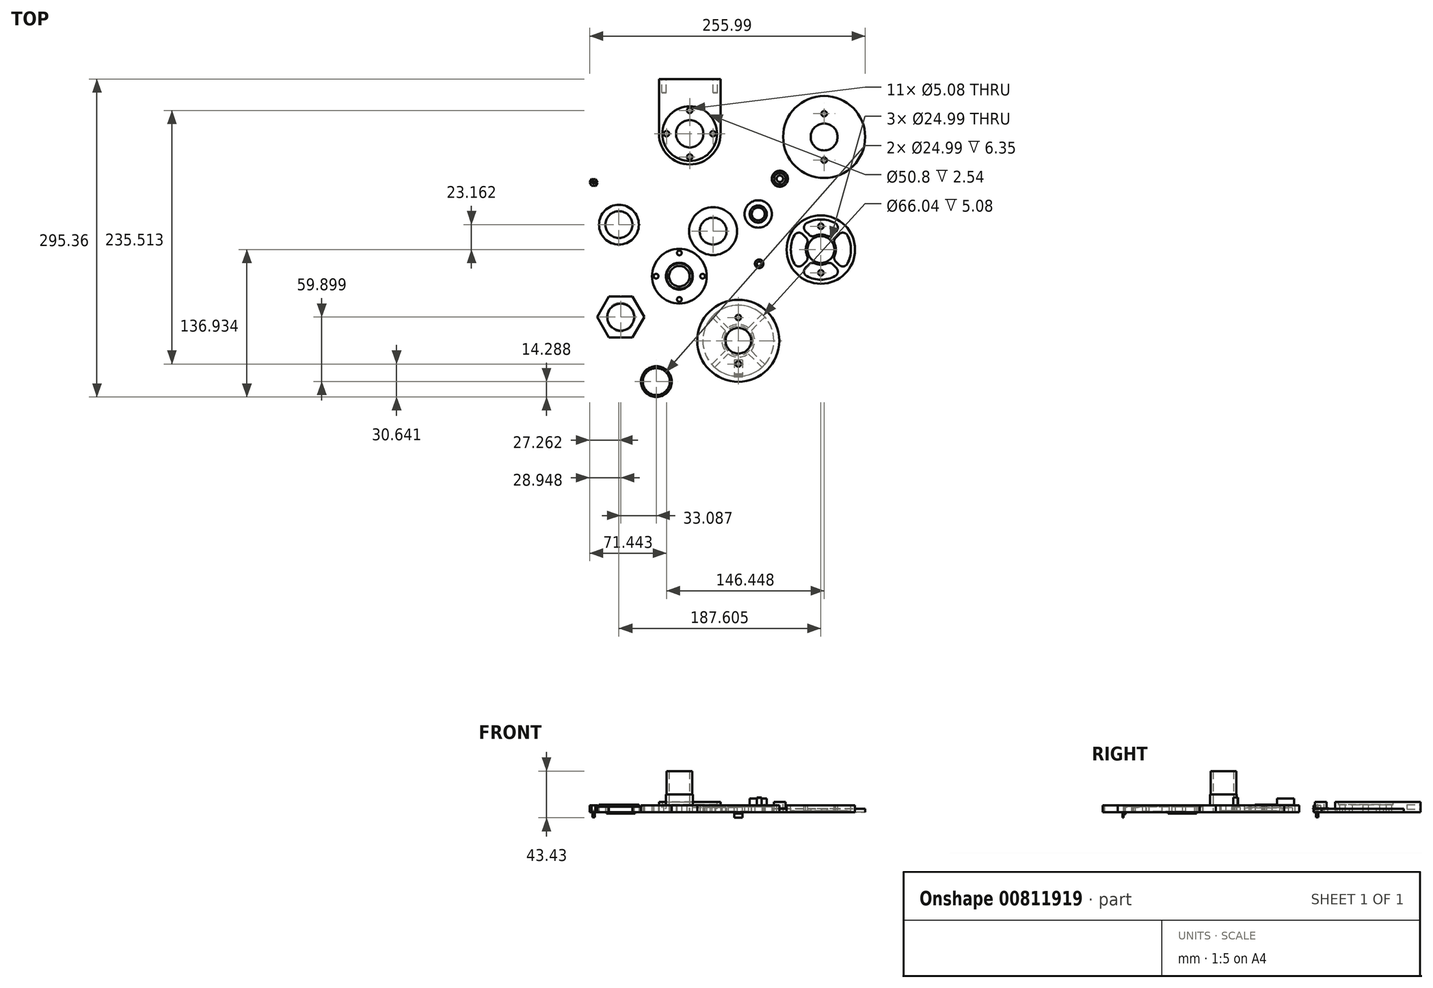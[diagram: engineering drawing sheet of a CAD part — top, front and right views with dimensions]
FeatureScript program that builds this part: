
annotation { "Feature Type Name" : "Feature", "Feature Type Description" : "" }
export const myFeature = defineFeature(function(context is Context, id is Id, definition is map)
    precondition{}
    {
        {
            var Q0;
            Q0=qCreatedBy(makeId("Top.planeOp"),FACE);
            var sketch = newSketch(context, id + "F0", { "sketchPlane" : qUnion([Q0])});
            skCircle(sketch, "E0", {"center": v(0, 0) * mm, "radius": 25.4 * mm});
            skSolve(sketch);
        }
        {
            var Q0;
            Q0=makeQuery(id+"F0.imprint","IMPRINT",FACE,{"disambiguationData":[TD([[makeQuery(id+"F0.imprint","IMPRINT",EDGE,{"derivedFrom":sQuery(id+"F0.wireOp",EDGE,"E0")}),1.0]])]});
            extrude(context, id + "F1", {"entities" : qUnion([Q0]), "depth" : 6.35 * mm});
        }
        {
            var Q0;
            Q0=makeQuery(id+"F1.opExtrude","CAP_FACE",FACE,{"disambiguationData":[OSD([sQuery(id+"F0.wireOp",EDGE,"E0")])],"isStart":false});
            var sketch = newSketch(context, id + "F2", { "sketchPlane" : qUnion([Q0])});
            skCircle(sketch, "E1", {"center": v(0, 0) * mm, "radius": 12.5 * mm});
            skSolve(sketch);
        }
        {
            var Q0;
            Q0=makeQuery(id+"F2.imprint","IMPRINT",FACE,{"disambiguationData":[TD([[makeQuery(id+"F2.imprint","IMPRINT",EDGE,{"derivedFrom":sQuery(id+"F2.wireOp",EDGE,"E1")}),1.0]])]});
            extrude(context, id + "F3", {"entities" : qUnion([Q0]), "operationType" : NewBodyOperationType.ADD, "depth" : 10.16 * mm});
        }
        {
            var Q0;
            Q0=makeQuery(id+"F3.opExtrude","CAP_FACE",FACE,{"disambiguationData":[OSD([sQuery(id+"F2.wireOp",EDGE,"E1")])],"isStart":false});
            var sketch = newSketch(context, id + "F4", { "sketchPlane" : qUnion([Q0])});
            skCircle(sketch, "E2", {"center": v(0, 0) * mm, "radius": 11.9 * mm});
            skSolve(sketch);
        }
        {
            var Q0;
            Q0=makeQuery(id+"F4.imprint","IMPRINT",FACE,{"disambiguationData":[TD([[makeQuery(id+"F4.imprint","IMPRINT",EDGE,{"derivedFrom":sQuery(id+"F4.wireOp",EDGE,"E2")}),1.0]])]});
            extrude(context, id + "F5", {"entities" : qUnion([Q0]), "operationType" : NewBodyOperationType.ADD, "depth" : 21.59 * mm});
        }
        {
            var Q0;
            Q0=makeQuery(id+"F1.opExtrude","CAP_FACE",FACE,{"disambiguationData":[OSD([sQuery(id+"F0.wireOp",EDGE,"E0")])],"isStart":true});
            var sketch = newSketch(context, id + "F6", { "sketchPlane" : qUnion([Q0])});
            skCircle(sketch, "E3", {"center": v(0, 0) * mm, "radius": 9.53 * mm});
            skSolve(sketch);
        }
        {
            var Q0;
            Q0=makeQuery(id+"F6.imprint","IMPRINT",FACE,{"disambiguationData":[TD([[makeQuery(id+"F6.imprint","IMPRINT",EDGE,{"derivedFrom":sQuery(id+"F6.wireOp",EDGE,"E3")}),1.0]])]});
            extrude(context, id + "F7", {"entities" : qUnion([Q0]), "operationType" : NewBodyOperationType.REMOVE, "endBound" : BoundingType.THROUGH_ALL, "oppositeDirection" : true, "depth" : 25.4 * mm});
        }
        {
            var Q0;
            Q0=makeQuery(id+"F1.opExtrude","CAP_FACE",FACE,{"disambiguationData":[OSD([sQuery(id+"F0.wireOp",EDGE,"E0")])],"isStart":true});
            var sketch = newSketch(context, id + "F8", { "sketchPlane" : qUnion([Q0])});
            skCircle(sketch, "E4", {"center": v(0, 0) * mm, "radius": 21.59 * mm, "construction": true});
            skCircle(sketch, "E5", {"center": v(0, -21.59) * mm, "radius": 2.16 * mm});
            skCircle(sketch, "E6", {"center": v(0, 21.59) * mm, "radius": 2.16 * mm});
            skCircle(sketch, "E7", {"center": v(-21.59, 0) * mm, "radius": 2.16 * mm});
            skCircle(sketch, "E8", {"center": v(21.59, 0) * mm, "radius": 2.16 * mm});
            skSolve(sketch);
        }
        {
            var Q0;
            {Q0=qUnion([makeQuery(id+"F8.imprint","IMPRINT",FACE,{"disambiguationData":[TD([[makeQuery(id+"F8.imprint","IMPRINT",EDGE,{"derivedFrom":sQuery(id+"F8.wireOp",EDGE,"E5")}),1.0]])]}),makeQuery(id+"F8.imprint","IMPRINT",FACE,{"disambiguationData":[TD([[makeQuery(id+"F8.imprint","IMPRINT",EDGE,{"derivedFrom":sQuery(id+"F8.wireOp",EDGE,"E8")}),1.0]])]}),makeQuery(id+"F8.imprint","IMPRINT",FACE,{"disambiguationData":[TD([[makeQuery(id+"F8.imprint","IMPRINT",EDGE,{"derivedFrom":sQuery(id+"F8.wireOp",EDGE,"E7")}),1.0]])]}),makeQuery(id+"F8.imprint","IMPRINT",FACE,{"disambiguationData":[TD([[makeQuery(id+"F8.imprint","IMPRINT",EDGE,{"derivedFrom":sQuery(id+"F8.wireOp",EDGE,"E6")}),1.0]])]})]);}
            extrude(context, id + "F9", {"entities" : qUnion([Q0]), "operationType" : NewBodyOperationType.REMOVE, "endBound" : BoundingType.THROUGH_ALL, "oppositeDirection" : true, "depth" : 25.4 * mm});
        }
        {
            var Q0;
            Q0=qCreatedBy(makeId("Top.planeOp"),FACE);
            var sketch = newSketch(context, id + "F10", { "sketchPlane" : qUnion([Q0])});
            skCircle(sketch, "E9", {"center": v(31.37, 41.87) * mm, "radius": 12.5 * mm});
            skCircle(sketch, "E10", {"center": v(31.37, 41.87) * mm, "radius": 22.23 * mm});
            skSolve(sketch);
        }
        {
            var Q0;
            Q0=makeQuery(id+"F10.imprint","IMPRINT",FACE,{"disambiguationData":[TD([[makeQuery(id+"F10.imprint","IMPRINT",EDGE,{"derivedFrom":sQuery(id+"F10.wireOp",EDGE,"E9")}),-1.0]])]});
            extrude(context, id + "F11", {"entities" : qUnion([Q0]), "depth" : 4 * mm});
        }
        {
            var Q0;
            Q0=qCreatedBy(makeId("Top.planeOp"),FACE);
            var sketch = newSketch(context, id + "F12", { "sketchPlane" : qUnion([Q0])});
            skCircle(sketch, "E11", {"center": v(-56.12, 47.92) * mm, "radius": 12.5 * mm});
            skCircle(sketch, "E12", {"center": v(-56.12, 47.92) * mm, "radius": 18.5 * mm});
            skSolve(sketch);
        }
        {
            var Q0;
            Q0=makeQuery(id+"F12.imprint","IMPRINT",FACE,{"disambiguationData":[TD([[makeQuery(id+"F12.imprint","IMPRINT",EDGE,{"derivedFrom":sQuery(id+"F12.wireOp",EDGE,"E11")}),-1.0]])]});
            extrude(context, id + "F13", {"entities" : qUnion([Q0]), "depth" : 7 * mm});
        }
        {
            var Q0;
            Q0=makeQuery(id+"F13.opExtrude","CAP_FACE",FACE,{"disambiguationData":[OSD([sQuery(id+"F12.wireOp",EDGE,"E11"),sQuery(id+"F12.wireOp",EDGE,"E12")])],"isStart":false});
            var Q1;
            Q1=makeQuery(id+"F13.opExtrude","SWEPT_FACE",FACE,{"disambiguationData":[OSD([sQuery(id+"F12.wireOp",EDGE,"E11")])]});
            var Q2;
            Q2=makeQuery(id+"F13.opExtrude","SWEPT_FACE",FACE,{"disambiguationData":[OSD([sQuery(id+"F12.wireOp",EDGE,"E12")])]});
            var Q3;
            Q3=makeQuery(id+"F13.opExtrude","CAP_FACE",FACE,{"disambiguationData":[OSD([sQuery(id+"F12.wireOp",EDGE,"E11"),sQuery(id+"F12.wireOp",EDGE,"E12")])],"isStart":true});
            fillet(context, id + "F14", {"entities" : qUnion([Q0, Q1, Q2, Q3]), "radius" : 0.64 * mm, "tangentPropagation" : true, "allowEdgeOverflow" : false});
        }
        {
            var Q0;
            Q0=qCreatedBy(makeId("Top.planeOp"),FACE);
            var sketch = newSketch(context, id + "F15", { "sketchPlane" : qUnion([Q0])});
            skLineSegment(sketch, "E13", {"start": v(-76.43, -38) * mm, "end": v(-65.43, -18.94) * mm});
            skLineSegment(sketch, "E14", {"start": v(-65.43, -18.94) * mm, "end": v(-43.43, -18.94) * mm});
            skLineSegment(sketch, "E15", {"start": v(-43.43, -18.94) * mm, "end": v(-32.44, -38) * mm});
            skLineSegment(sketch, "E16", {"start": v(-32.44, -38) * mm, "end": v(-43.43, -57.04) * mm});
            skLineSegment(sketch, "E17", {"start": v(-43.43, -57.04) * mm, "end": v(-65.43, -57.04) * mm});
            skLineSegment(sketch, "E18", {"start": v(-65.43, -57.04) * mm, "end": v(-76.43, -38) * mm});
            skSolve(sketch);
        }
        {
            var Q0;
            Q0=makeQuery(id+"F15.imprint","IMPRINT",FACE,{"disambiguationData":[TD([[makeQuery(id+"F15.imprint","IMPRINT",EDGE,{"derivedFrom":sQuery(id+"F15.wireOp",EDGE,"E13")}),-1.0]])]});
            extrude(context, id + "F16", {"entities" : qUnion([Q0]), "depth" : 5.08 * mm});
        }
        {
            var Q0;
            Q0=makeQuery(id+"F16.opExtrude","CAP_FACE",FACE,{"disambiguationData":[OSD([sQuery(id+"F15.wireOp",EDGE,"E13"),sQuery(id+"F15.wireOp",EDGE,"E14"),sQuery(id+"F15.wireOp",EDGE,"E15"),sQuery(id+"F15.wireOp",EDGE,"E16"),sQuery(id+"F15.wireOp",EDGE,"E17"),sQuery(id+"F15.wireOp",EDGE,"E18")])],"isStart":true});
            var sketch = newSketch(context, id + "F17", { "sketchPlane" : qUnion([Q0])});
            skCircle(sketch, "E19", {"center": v(-54.43, 38) * mm, "radius": 12.5 * mm});
            skSolve(sketch);
        }
        {
            var Q0;
            Q0=makeQuery(id+"F17.imprint","IMPRINT",FACE,{"disambiguationData":[TD([[makeQuery(id+"F17.imprint","IMPRINT",EDGE,{"derivedFrom":sQuery(id+"F17.wireOp",EDGE,"E19")}),1.0]])]});
            extrude(context, id + "F18", {"entities" : qUnion([Q0]), "operationType" : NewBodyOperationType.REMOVE, "endBound" : BoundingType.THROUGH_ALL, "oppositeDirection" : true, "depth" : 25.4 * mm});
        }
        {
            var Q0;
            Q0=makeQuery(id+"F16.opExtrude","CAP_FACE",FACE,{"disambiguationData":[OSD([sQuery(id+"F15.wireOp",EDGE,"E13"),sQuery(id+"F15.wireOp",EDGE,"E14"),sQuery(id+"F15.wireOp",EDGE,"E15"),sQuery(id+"F15.wireOp",EDGE,"E16"),sQuery(id+"F15.wireOp",EDGE,"E17"),sQuery(id+"F15.wireOp",EDGE,"E18")])],"isStart":true});
            var sketch = newSketch(context, id + "F19", { "sketchPlane" : qUnion([Q0])});
            skCircle(sketch, "E20", {"center": v(-54.43, 38) * mm, "radius": 13.34 * mm});
            skSolve(sketch);
        }
        {
            var Q0;
            Q0=makeQuery(id+"F19.imprint","IMPRINT",FACE,{"disambiguationData":[TD([[makeQuery(id+"F19.imprint","IMPRINT",EDGE,{"derivedFrom":sQuery(id+"F19.wireOp",EDGE,"E20")}),1.0]])]});
            extrude(context, id + "F20", {"entities" : qUnion([Q0]), "operationType" : NewBodyOperationType.ADD, "depth" : 1.27 * mm});
        }
        {
            var Q0;
            Q0=qCreatedBy(makeId("Top.planeOp"),FACE);
            var sketch = newSketch(context, id + "F21", { "sketchPlane" : qUnion([Q0])});
            skCircle(sketch, "E21", {"center": v(54.8, -59.95) * mm, "radius": 11.9 * mm});
            skCircle(sketch, "E22", {"center": v(54.8, -59.95) * mm, "radius": 38.1 * mm});
            skSolve(sketch);
        }
        {
            var Q0;
            Q0=makeQuery(id+"F21.imprint","IMPRINT",FACE,{"disambiguationData":[TD([[makeQuery(id+"F21.imprint","IMPRINT",EDGE,{"derivedFrom":sQuery(id+"F21.wireOp",EDGE,"E21")}),-1.0]])]});
            extrude(context, id + "F22", {"entities" : qUnion([Q0]), "depth" : 6.35 * mm});
        }
        {
            var Q0;
            Q0=qCreatedBy(makeId("Top.planeOp"),FACE);
            var sketch = newSketch(context, id + "F23", { "sketchPlane" : qUnion([Q0])});
            skCircle(sketch, "E23", {"center": v(73.3, 57.82) * mm, "radius": 12.7 * mm});
            skSolve(sketch);
        }
        {
            var Q0;
            Q0=makeQuery(id+"F23.imprint","IMPRINT",FACE,{"disambiguationData":[TD([[makeQuery(id+"F23.imprint","IMPRINT",EDGE,{"derivedFrom":sQuery(id+"F23.wireOp",EDGE,"E23")}),1.0]])]});
            extrude(context, id + "F24", {"entities" : qUnion([Q0]), "depth" : 6.35 * mm});
        }
        {
            var Q0;
            Q0=makeQuery(id+"F24.opExtrude","CAP_FACE",FACE,{"disambiguationData":[OSD([sQuery(id+"F23.wireOp",EDGE,"E23")])],"isStart":false});
            var sketch = newSketch(context, id + "F25", { "sketchPlane" : qUnion([Q0])});
            skCircle(sketch, "E24", {"center": v(73.3, 57.82) * mm, "radius": 7.94 * mm});
            skSolve(sketch);
        }
        {
            var Q0;
            Q0=makeQuery(id+"F25.imprint","IMPRINT",FACE,{"disambiguationData":[TD([[makeQuery(id+"F25.imprint","IMPRINT",EDGE,{"derivedFrom":sQuery(id+"F25.wireOp",EDGE,"E24")}),1.0]])]});
            extrude(context, id + "F26", {"entities" : qUnion([Q0]), "operationType" : NewBodyOperationType.ADD, "depth" : 6.35 * mm});
        }
        {
            var Q0;
            Q0=qCreatedBy(makeId("Top.planeOp"),FACE);
            var sketch = newSketch(context, id + "F27", { "sketchPlane" : qUnion([Q0])});
            skCircle(sketch, "E25", {"center": v(-21.34, -97.9) * mm, "radius": 12.5 * mm});
            skCircle(sketch, "E26", {"center": v(-21.34, -97.9) * mm, "radius": 14.29 * mm});
            skSolve(sketch);
        }
        {
            var Q0;
            Q0=makeQuery(id+"F27.imprint","IMPRINT",FACE,{"disambiguationData":[TD([[makeQuery(id+"F27.imprint","IMPRINT",EDGE,{"derivedFrom":sQuery(id+"F27.wireOp",EDGE,"E25")}),-1.0]])]});
            extrude(context, id + "F28", {"entities" : qUnion([Q0]), "depth" : 6.35 * mm});
        }
        {
            var Q0;
            Q0=makeQuery(id+"F26.opExtrude","CAP_FACE",FACE,{"disambiguationData":[OSD([sQuery(id+"F25.wireOp",EDGE,"E24")])],"isStart":false});
            var sketch = newSketch(context, id + "F29", { "sketchPlane" : qUnion([Q0])});
            skCircle(sketch, "E27", {"center": v(73.3, 57.82) * mm, "radius": 6 * mm});
            skSolve(sketch);
        }
        {
            var Q0;
            Q0=makeQuery(id+"F29.imprint","IMPRINT",FACE,{"disambiguationData":[TD([[makeQuery(id+"F29.imprint","IMPRINT",EDGE,{"derivedFrom":sQuery(id+"F29.wireOp",EDGE,"E27")}),1.0]])]});
            extrude(context, id + "F30", {"entities" : qUnion([Q0]), "operationType" : NewBodyOperationType.REMOVE, "endBound" : BoundingType.THROUGH_ALL, "oppositeDirection" : true, "depth" : 25.4 * mm});
        }
        {
            var Q0;
            Q0=qCreatedBy(makeId("Top.planeOp"),FACE);
            var sketch = newSketch(context, id + "F31", { "sketchPlane" : qUnion([Q0])});
            skCircle(sketch, "E28", {"center": v(9.65, 132.38) * mm, "radius": 28.58 * mm});
            skCircle(sketch, "E29", {"center": v(9.65, 132.38) * mm, "radius": 12.7 * mm});
            skLineSegment(sketch, "E30.bottom", {"start": v(-18.92, 132.38) * mm, "end": v(38.23, 132.38) * mm});
            skLineSegment(sketch, "E30.top", {"start": v(-18.92, 183.18) * mm, "end": v(38.23, 183.18) * mm});
            skLineSegment(sketch, "E30.left", {"start": v(-18.92, 132.38) * mm, "end": v(-18.92, 183.18) * mm});
            skLineSegment(sketch, "E30.right", {"start": v(38.23, 132.38) * mm, "end": v(38.23, 183.18) * mm});
            skSolve(sketch);
        }
        {
            var Q0;
            {var subQ3=sQuery(id+"F31.wireOp",EDGE,"E30.bottom");var subQ7=sQuery(id+"F31.wireOp",EDGE,"E29");var subQ10=makeQuery(id+"F31.imprint","INTERSECT",VERTEX,{"disambiguationData":[OD(0.0)],"derivedFrom":[subQ7,subQ3]});Q0=qUnion([makeQuery(id+"F31.imprint","IMPRINT",FACE,{"disambiguationData":[TD([[makeQuery(id+"F31.imprint","IMPRINT",EDGE,{"derivedFrom":sQuery(id+"F31.wireOp",EDGE,"E30.top")}),-1.0]])]}),makeQuery(id+"F31.imprint","IMPRINT",FACE,{"disambiguationData":[TD([[makeQuery(id+"F31.imprint","IMPRINT",EDGE,{"disambiguationData":[TD([[subQ10,1.0]])],"derivedFrom":subQ7}),-1.0]])]}),makeQuery(id+"F31.imprint","IMPRINT",FACE,{"disambiguationData":[TD([[makeQuery(id+"F31.imprint","IMPRINT",EDGE,{"disambiguationData":[TD([[subQ10,-1.0]])],"derivedFrom":subQ7}),-1.0]])]})]);}
            extrude(context, id + "F32", {"entities" : qUnion([Q0]), "depth" : 9.52 * mm});
        }
        {
            var Q0;
            Q0=makeQuery(id+"F32.opExtrude","CAP_FACE",FACE,{"disambiguationData":[OSD([sQuery(id+"F31.wireOp",EDGE,"E28"),sQuery(id+"F31.wireOp",EDGE,"E29"),sQuery(id+"F31.wireOp",EDGE,"E30.top"),sQuery(id+"F31.wireOp",EDGE,"E30.left"),sQuery(id+"F31.wireOp",EDGE,"E30.right")])],"isStart":false});
            var sketch = newSketch(context, id + "F33", { "sketchPlane" : qUnion([Q0])});
            skCircle(sketch, "E31", {"center": v(9.65, 132.38) * mm, "radius": 25.4 * mm});
            skSolve(sketch);
        }
        {
            var Q0;
            Q0=makeQuery(id+"F33.imprint","IMPRINT",FACE,{"disambiguationData":[TD([[makeQuery(id+"F33.imprint","IMPRINT",EDGE,{"derivedFrom":sQuery(id+"F33.wireOp",EDGE,"E31")}),1.0]])]});
            extrude(context, id + "F34", {"entities" : qUnion([Q0]), "operationType" : NewBodyOperationType.REMOVE, "oppositeDirection" : true, "depth" : 2.54 * mm});
        }
        {
            var Q0;
            Q0=makeQuery(id+"F34.boolean.opBoolean","COPY",FACE,{"derivedFrom":makeQuery(id+"F34.opExtrude","CAP_FACE",FACE,{"disambiguationData":[OSD([sQuery(id+"F31.wireOp",EDGE,"E29"),sQuery(id+"F33.wireOp",EDGE,"E31")])],"isStart":false})});
            var sketch = newSketch(context, id + "F35", { "sketchPlane" : qUnion([Q0])});
            skCircle(sketch, "E32", {"center": v(9.65, 132.38) * mm, "radius": 21.59 * mm, "construction": true});
            skCircle(sketch, "E33", {"center": v(9.65, 153.97) * mm, "radius": 2.54 * mm});
            skCircle(sketch, "E34", {"center": v(31.24, 132.38) * mm, "radius": 2.54 * mm});
            skCircle(sketch, "E35", {"center": v(9.65, 110.8) * mm, "radius": 2.54 * mm});
            skCircle(sketch, "E36", {"center": v(-11.94, 132.38) * mm, "radius": 2.54 * mm});
            skLineSegment(sketch, "E37", {"start": v(-11.94, 132.38) * mm, "end": v(31.24, 132.38) * mm, "construction": true});
            skLineSegment(sketch, "E38", {"start": v(9.65, 153.97) * mm, "end": v(9.65, 110.8) * mm, "construction": true});
            skSolve(sketch);
        }
        {
            var Q0;
            {Q0=qUnion([makeQuery(id+"F35.imprint","IMPRINT",FACE,{"disambiguationData":[TD([[makeQuery(id+"F35.imprint","IMPRINT",EDGE,{"derivedFrom":sQuery(id+"F35.wireOp",EDGE,"E33")}),1.0]])]}),makeQuery(id+"F35.imprint","IMPRINT",FACE,{"disambiguationData":[TD([[makeQuery(id+"F35.imprint","IMPRINT",EDGE,{"derivedFrom":sQuery(id+"F35.wireOp",EDGE,"E34")}),1.0]])]}),makeQuery(id+"F35.imprint","IMPRINT",FACE,{"disambiguationData":[TD([[makeQuery(id+"F35.imprint","IMPRINT",EDGE,{"derivedFrom":sQuery(id+"F35.wireOp",EDGE,"E35")}),1.0]])]}),makeQuery(id+"F35.imprint","IMPRINT",FACE,{"disambiguationData":[TD([[makeQuery(id+"F35.imprint","IMPRINT",EDGE,{"derivedFrom":sQuery(id+"F35.wireOp",EDGE,"E36")}),1.0]])]})]);}
            extrude(context, id + "F36", {"entities" : qUnion([Q0]), "operationType" : NewBodyOperationType.REMOVE, "endBound" : BoundingType.THROUGH_ALL, "oppositeDirection" : true, "depth" : 25.4 * mm});
        }
        {
            var Q0;
            Q0=makeQuery(id+"F32.opExtrude","SWEPT_FACE",FACE,{"disambiguationData":[OSD([sQuery(id+"F31.wireOp",EDGE,"E30.top")])]});
            var sketch = newSketch(context, id + "F37", { "sketchPlane" : qUnion([Q0])});
            skCircle(sketch, "E39", {"center": v(14.16, 4.76) * mm, "radius": 2.16 * mm});
            skCircle(sketch, "E40", {"center": v(-33.47, 4.76) * mm, "radius": 2.16 * mm});
            skSolve(sketch);
        }
        {
            var Q0;
            {Q0=qUnion([makeQuery(id+"F37.imprint","IMPRINT",FACE,{"disambiguationData":[TD([[makeQuery(id+"F37.imprint","IMPRINT",EDGE,{"derivedFrom":sQuery(id+"F37.wireOp",EDGE,"E39")}),1.0]])]}),makeQuery(id+"F37.imprint","IMPRINT",FACE,{"disambiguationData":[TD([[makeQuery(id+"F37.imprint","IMPRINT",EDGE,{"derivedFrom":sQuery(id+"F37.wireOp",EDGE,"E40")}),1.0]])]})]);}
            extrude(context, id + "F38", {"entities" : qUnion([Q0]), "operationType" : NewBodyOperationType.REMOVE, "oppositeDirection" : true, "depth" : 12.7 * mm});
        }
        {
            var Q0;
            Q0=qCreatedBy(makeId("Top.planeOp"),FACE);
            var sketch = newSketch(context, id + "F39", { "sketchPlane" : qUnion([Q0])});
            skCircle(sketch, "E41", {"center": v(74.17, 11.52) * mm, "radius": 4 * mm});
            skSolve(sketch);
        }
        {
            var Q0;
            Q0=makeQuery(id+"F39.imprint","IMPRINT",FACE,{"disambiguationData":[TD([[makeQuery(id+"F39.imprint","IMPRINT",EDGE,{"derivedFrom":sQuery(id+"F39.wireOp",EDGE,"E41")}),1.0]])]});
            extrude(context, id + "F40", {"entities" : qUnion([Q0]), "depth" : 4.7 * mm});
        }
        {
            var Q0;
            Q0=makeQuery(id+"F40.opExtrude","CAP_FACE",FACE,{"disambiguationData":[OSD([sQuery(id+"F39.wireOp",EDGE,"E41")])],"isStart":false});
            var sketch = newSketch(context, id + "F41", { "sketchPlane" : qUnion([Q0])});
            skCircle(sketch, "E42", {"center": v(74.17, 11.52) * mm, "radius": 2.16 * mm});
            skSolve(sketch);
        }
        {
            var Q0;
            Q0=makeQuery(id+"F41.imprint","IMPRINT",FACE,{"disambiguationData":[TD([[makeQuery(id+"F41.imprint","IMPRINT",EDGE,{"derivedFrom":sQuery(id+"F41.wireOp",EDGE,"E42")}),1.0]])]});
            extrude(context, id + "F42", {"entities" : qUnion([Q0]), "operationType" : NewBodyOperationType.ADD, "depth" : 8.9 * mm});
        }
        {
            var Q0;
            Q0=makeQuery(id+"F22.opExtrude","CAP_FACE",FACE,{"disambiguationData":[OSD([sQuery(id+"F21.wireOp",EDGE,"E21"),sQuery(id+"F21.wireOp",EDGE,"E22")])],"isStart":false});
            var sketch = newSketch(context, id + "F43", { "sketchPlane" : qUnion([Q0])});
            skCircle(sketch, "E43", {"center": v(54.8, -59.95) * mm, "radius": 21.59 * mm, "construction": true});
            skCircle(sketch, "E44", {"center": v(54.8, -38.36) * mm, "radius": 2.54 * mm});
            skCircle(sketch, "E45", {"center": v(54.8, -81.54) * mm, "radius": 2.54 * mm});
            skSolve(sketch);
        }
        {
            var Q0;
            {Q0=qUnion([makeQuery(id+"F43.imprint","IMPRINT",FACE,{"disambiguationData":[TD([[makeQuery(id+"F43.imprint","IMPRINT",EDGE,{"derivedFrom":sQuery(id+"F43.wireOp",EDGE,"E45")}),1.0]])]}),makeQuery(id+"F43.imprint","IMPRINT",FACE,{"disambiguationData":[TD([[makeQuery(id+"F43.imprint","IMPRINT",EDGE,{"derivedFrom":sQuery(id+"F43.wireOp",EDGE,"E44")}),1.0]])]})]);}
            extrude(context, id + "F44", {"entities" : qUnion([Q0]), "operationType" : NewBodyOperationType.REMOVE, "endBound" : BoundingType.THROUGH_ALL, "oppositeDirection" : true, "depth" : 25.4 * mm});
        }
        {
            var Q0;
            Q0=makeQuery(id+"F22.opExtrude","CAP_FACE",FACE,{"disambiguationData":[OSD([sQuery(id+"F21.wireOp",EDGE,"E21"),sQuery(id+"F21.wireOp",EDGE,"E22")])],"isStart":true});
            var sketch = newSketch(context, id + "F45", { "sketchPlane" : qUnion([Q0])});
            skArc(sketch, "E46", {"start": v(30.13, 81.91) * mm, "mid": v(21.77, 59.95) * mm, "end": v(30.13, 37.99) * mm});
            skArc(sketch, "E47", {"start": v(42.75, 69.3) * mm, "mid": v(39.55, 59.95) * mm, "end": v(42.75, 50.6) * mm});
            skLineSegment(sketch, "E48.rect.bottom", {"start": v(78.14, 83.3) * mm, "end": v(31.44, 83.3) * mm, "construction": true});
            skLineSegment(sketch, "E48.rect.top", {"start": v(78.14, 36.6) * mm, "end": v(31.44, 36.6) * mm, "construction": true});
            skLineSegment(sketch, "E48.rect.left", {"start": v(78.14, 83.3) * mm, "end": v(78.14, 36.6) * mm, "construction": true});
            skLineSegment(sketch, "E48.rect.right", {"start": v(31.44, 83.3) * mm, "end": v(31.44, 36.6) * mm, "construction": true});
            skLineSegment(sketch, "E49", {"start": v(31.44, 83.3) * mm, "end": v(78.14, 36.6) * mm, "construction": true});
            skLineSegment(sketch, "E50", {"start": v(31.44, 36.6) * mm, "end": v(78.14, 83.3) * mm, "construction": true});
            skLineSegment(sketch, "E51.0", {"start": v(30.1, 81.95) * mm, "end": v(42.75, 69.3) * mm});
            skLineSegment(sketch, "E52.0", {"start": v(32.79, 35.25) * mm, "end": v(45.45, 47.91) * mm});
            skLineSegment(sketch, "E53.0", {"start": v(32.79, 84.64) * mm, "end": v(45.45, 71.99) * mm});
            skLineSegment(sketch, "E54.0", {"start": v(30.1, 37.95) * mm, "end": v(42.75, 50.6) * mm});
            skLineSegment(sketch, "E55.trimOffspring", {"start": v(54.8, 62.64) * mm, "end": v(57.48, 59.95) * mm});
            skLineSegment(sketch, "E56.trimOffspring", {"start": v(52.1, 59.95) * mm, "end": v(54.8, 57.25) * mm});
            skLineSegment(sketch, "E57.trimOffspring", {"start": v(64.14, 71.99) * mm, "end": v(76.8, 84.64) * mm});
            skLineSegment(sketch, "E58.trimOffspring", {"start": v(66.83, 69.3) * mm, "end": v(79.49, 81.95) * mm});
            skLineSegment(sketch, "E59.trimOffspring", {"start": v(66.83, 50.6) * mm, "end": v(79.49, 37.95) * mm});
            skLineSegment(sketch, "E60.trimOffspring", {"start": v(64.14, 47.91) * mm, "end": v(76.8, 35.25) * mm});
            skLineSegment(sketch, "E61.trimOffspring", {"start": v(54.8, 57.25) * mm, "end": v(57.48, 59.95) * mm});
            skLineSegment(sketch, "E62.trimOffspring", {"start": v(52.1, 59.95) * mm, "end": v(54.8, 62.64) * mm});
            skArc(sketch, "E63.trimOffspring", {"start": v(64.14, 71.99) * mm, "mid": v(54.8, 75.19) * mm, "end": v(45.45, 71.99) * mm});
            skArc(sketch, "E64.trimOffspring", {"start": v(66.83, 50.6) * mm, "mid": v(70.03, 59.95) * mm, "end": v(66.83, 69.3) * mm});
            skArc(sketch, "E65.trimOffspring", {"start": v(45.45, 47.91) * mm, "mid": v(54.8, 44.7) * mm, "end": v(64.14, 47.91) * mm});
            skArc(sketch, "E66.trimOffspring", {"start": v(76.75, 84.6) * mm, "mid": v(54.8, 92.97) * mm, "end": v(32.83, 84.6) * mm});
            skArc(sketch, "E67.trimOffspring", {"start": v(32.83, 35.3) * mm, "mid": v(54.8, 26.93) * mm, "end": v(76.75, 35.3) * mm});
            skArc(sketch, "E68.trimOffspring", {"start": v(79.45, 37.99) * mm, "mid": v(87.81, 59.95) * mm, "end": v(79.45, 81.91) * mm});
            skSolve(sketch);
        }
        {
            var Q0;
            {var subQ2=sQuery(id+"F45.wireOp",EDGE,"E65.trimOffspring");var subQ6=sQuery(id+"F45.wireOp",EDGE,"E64.trimOffspring");var subQ10=sQuery(id+"F45.wireOp",EDGE,"E63.trimOffspring");var subQ15=sQuery(id+"F45.wireOp",EDGE,"E46");Q0=qUnion([makeQuery(id+"F45.imprint","IMPRINT",FACE,{"disambiguationData":[TD([[makeQuery(id+"F45.imprint","IMPRINT",EDGE,{"derivedFrom":sQuery(id+"F45.wireOp",EDGE,"E55.trimOffspring")}),-1.0]])]}),makeQuery(id+"F45.imprint","IMPRINT",FACE,{"disambiguationData":[TD([[makeQuery(id+"F45.imprint","IMPRINT",EDGE,{"derivedFrom":subQ2}),-1.0]])]}),makeQuery(id+"F45.imprint","IMPRINT",FACE,{"disambiguationData":[TD([[makeQuery(id+"F45.imprint","IMPRINT",EDGE,{"derivedFrom":subQ6}),-1.0]])]}),makeQuery(id+"F45.imprint","IMPRINT",FACE,{"disambiguationData":[TD([[makeQuery(id+"F45.imprint","IMPRINT",EDGE,{"derivedFrom":subQ10}),-1.0]])]}),makeQuery(id+"F45.imprint","IMPRINT",FACE,{"disambiguationData":[TD([[makeQuery(id+"F45.imprint","IMPRINT",EDGE,{"derivedFrom":subQ15}),1.0]])]})]);}
            extrude(context, id + "F46", {"entities" : qUnion([Q0]), "operationType" : NewBodyOperationType.REMOVE, "oppositeDirection" : true, "depth" : 5.08 * mm});
        }
        {
            var Q0;
            Q0=makeQuery(id+"F22.opExtrude","CAP_FACE",FACE,{"disambiguationData":[OSD([sQuery(id+"F21.wireOp",EDGE,"E21"),sQuery(id+"F21.wireOp",EDGE,"E22")])],"isStart":true});
            var sketch = newSketch(context, id + "F47", { "sketchPlane" : qUnion([Q0])});
            skCircle(sketch, "E69", {"center": v(54.8, 59.95) * mm, "radius": 13.65 * mm});
            skCircle(sketch, "E70", {"center": v(54.8, 59.95) * mm, "radius": 33.02 * mm});
            skSolve(sketch);
        }
        {
            var Q0;
            {var subQ4=makeQuery(id+"F47.imprint","IMPRINT",EDGE,{"derivedFrom":makeQuery(id+"F46.boolean.opBoolean","COPY",EDGE,{"derivedFrom":makeQuery(id+"F46.opExtrude","CAP_EDGE",EDGE,{"disambiguationData":[OSD([sQuery(id+"F45.wireOp",EDGE,"E47")])],"isStart":true})})});var subQ11=makeQuery(id+"F46.boolean.opBoolean","COPY",EDGE,{"derivedFrom":makeQuery(id+"F46.opExtrude","CAP_EDGE",EDGE,{"disambiguationData":[OSD([sQuery(id+"F45.wireOp",EDGE,"E58.trimOffspring")])],"isStart":true})});var subQ12=makeQuery(id+"F47.imprint","IMPRINT",EDGE,{"derivedFrom":subQ11});var subQ18=makeQuery(id+"F46.boolean.opBoolean","COPY",EDGE,{"derivedFrom":makeQuery(id+"F46.opExtrude","CAP_EDGE",EDGE,{"disambiguationData":[OSD([sQuery(id+"F45.wireOp",EDGE,"E52.0")])],"isStart":true})});var subQ19=makeQuery(id+"F47.imprint","IMPRINT",EDGE,{"derivedFrom":subQ18});var subQ25=makeQuery(id+"F46.boolean.opBoolean","COPY",EDGE,{"derivedFrom":makeQuery(id+"F46.opExtrude","CAP_EDGE",EDGE,{"disambiguationData":[OSD([sQuery(id+"F45.wireOp",EDGE,"E53.0")])],"isStart":true})});var subQ26=makeQuery(id+"F47.imprint","IMPRINT",EDGE,{"derivedFrom":subQ25});Q0=qUnion([makeQuery(id+"F47.imprint","IMPRINT",FACE,{"disambiguationData":[TD([[subQ4,-1.0]])]}),makeQuery(id+"F47.imprint","IMPRINT",FACE,{"disambiguationData":[TD([[subQ12,-1.0]])]}),makeQuery(id+"F47.imprint","IMPRINT",FACE,{"disambiguationData":[TD([[subQ19,-1.0]])]}),makeQuery(id+"F47.imprint","IMPRINT",FACE,{"disambiguationData":[TD([[subQ26,1.0]])]}),makeQuery(id+"F47.imprint","IMPRINT",FACE,{"disambiguationData":[TD([[makeQuery(id+"F47.imprint","IMPRINT",EDGE,{"derivedFrom":sQuery(id+"F47.wireOp",EDGE,"E69")}),-1.0]])]})]);}
            extrude(context, id + "F48", {"entities" : qUnion([Q0]), "operationType" : NewBodyOperationType.REMOVE, "oppositeDirection" : true, "depth" : 0.5 * mm});
        }
        {
            var Q0;
            Q0=qCreatedBy(makeId("Top.planeOp"),FACE);
            var sketch = newSketch(context, id + "F49", { "sketchPlane" : qUnion([Q0])});
            skCircle(sketch, "E71", {"center": v(131.49, 24.75) * mm, "radius": 31.75 * mm});
            skCircle(sketch, "E72", {"center": v(131.49, 24.75) * mm, "radius": 12.5 * mm});
            skSolve(sketch);
        }
        {
            var Q0;
            Q0=makeQuery(id+"F49.imprint","IMPRINT",FACE,{"disambiguationData":[TD([[makeQuery(id+"F49.imprint","IMPRINT",EDGE,{"derivedFrom":sQuery(id+"F49.wireOp",EDGE,"E71")}),1.0]])]});
            extrude(context, id + "F50", {"entities" : qUnion([Q0]), "depth" : 6.35 * mm});
        }
        {
            var Q0;
            Q0=makeQuery(id+"F50.opExtrude","CAP_FACE",FACE,{"disambiguationData":[OSD([sQuery(id+"F49.wireOp",EDGE,"E71"),sQuery(id+"F49.wireOp",EDGE,"E72")])],"isStart":false});
            var sketch = newSketch(context, id + "F51", { "sketchPlane" : qUnion([Q0])});
            skArc(sketch, "E73", {"start": v(106.83, 37.9) * mm, "mid": v(103.55, 24.75) * mm, "end": v(106.83, 11.6) * mm});
            skLineSegment(sketch, "E74", {"start": v(131.49, 61.47) * mm, "end": v(131.49, -13.2) * mm, "construction": true});
            skCircle(sketch, "E75", {"center": v(131.49, 24.75) * mm, "radius": 21.59 * mm, "construction": true});
            skLineSegment(sketch, "E76", {"start": v(99.53, 56.7) * mm, "end": v(165.48, -9.24) * mm, "construction": true});
            skLineSegment(sketch, "E77", {"start": v(99.82, -6.91) * mm, "end": v(162.98, 56.25) * mm, "construction": true});
            skLineSegment(sketch, "E78.0", {"start": v(114.5, 39.04) * mm, "end": v(117.73, 35.82) * mm});
            skLineSegment(sketch, "E79.0", {"start": v(117.2, 7.77) * mm, "end": v(120.43, 11) * mm});
            skLineSegment(sketch, "E80.0", {"start": v(114.5, 10.47) * mm, "end": v(117.73, 13.7) * mm});
            skLineSegment(sketch, "E81.0", {"start": v(117.2, 41.74) * mm, "end": v(120.43, 38.51) * mm});
            skArc(sketch, "E82.trimOffspring", {"start": v(144.63, 49.4) * mm, "mid": v(131.49, 52.7) * mm, "end": v(118.34, 49.4) * mm});
            skArc(sketch, "E83.trimOffspring", {"start": v(156.14, 11.6) * mm, "mid": v(159.43, 24.75) * mm, "end": v(156.14, 37.9) * mm});
            skArc(sketch, "E84.trimOffspring", {"start": v(118.34, 0.1) * mm, "mid": v(131.49, -3.19) * mm, "end": v(144.63, 0.1) * mm});
            skPoint(sketch, "E85.visualSharp", {"position": v(113.12, 45.81) * mm});
            skArc(sketch, "E85.filletArc", {"start": v(118.34, 49.4) * mm, "mid": v(115.84, 45.86) * mm, "end": v(117.2, 41.74) * mm});
            skPoint(sketch, "E86.visualSharp", {"position": v(149.85, 45.81) * mm});
            skArc(sketch, "E86.filletArc", {"start": v(145.78, 41.74) * mm, "mid": v(147.14, 45.86) * mm, "end": v(144.63, 49.4) * mm});
            skPoint(sketch, "E87.visualSharp", {"position": v(152.55, 43.12) * mm});
            skArc(sketch, "E87.filletArc", {"start": v(156.14, 37.9) * mm, "mid": v(152.6, 40.4) * mm, "end": v(148.47, 39.04) * mm});
            skPoint(sketch, "E88.visualSharp", {"position": v(152.55, 6.4) * mm});
            skArc(sketch, "E88.filletArc", {"start": v(148.47, 10.47) * mm, "mid": v(152.6, 9.1) * mm, "end": v(156.14, 11.6) * mm});
            skPoint(sketch, "E89.visualSharp", {"position": v(149.85, 3.7) * mm});
            skArc(sketch, "E89.filletArc", {"start": v(144.63, 0.1) * mm, "mid": v(147.14, 3.65) * mm, "end": v(145.78, 7.77) * mm});
            skPoint(sketch, "E90.visualSharp", {"position": v(113.12, 3.7) * mm});
            skArc(sketch, "E90.filletArc", {"start": v(117.2, 7.77) * mm, "mid": v(115.84, 3.65) * mm, "end": v(118.34, 0.1) * mm});
            skPoint(sketch, "E91.visualSharp", {"position": v(110.43, 6.4) * mm});
            skArc(sketch, "E91.filletArc", {"start": v(106.83, 11.6) * mm, "mid": v(110.38, 9.1) * mm, "end": v(114.5, 10.47) * mm});
            skPoint(sketch, "E92.visualSharp", {"position": v(110.43, 43.12) * mm});
            skArc(sketch, "E92.filletArc", {"start": v(114.5, 39.04) * mm, "mid": v(110.38, 40.4) * mm, "end": v(106.83, 37.9) * mm});
            skArc(sketch, "E93", {"start": v(125.8, 12) * mm, "mid": v(131.49, 10.78) * mm, "end": v(137.17, 12) * mm});
            skLineSegment(sketch, "E94.trimOffspring", {"start": v(142.55, 38.51) * mm, "end": v(145.78, 41.74) * mm});
            skLineSegment(sketch, "E95.trimOffspring", {"start": v(145.24, 35.82) * mm, "end": v(148.47, 39.04) * mm});
            skLineSegment(sketch, "E96.trimOffspring", {"start": v(145.24, 13.7) * mm, "end": v(148.47, 10.47) * mm});
            skLineSegment(sketch, "E97.trimOffspring", {"start": v(142.55, 11) * mm, "end": v(145.78, 7.77) * mm});
            skArc(sketch, "E98.trimOffspring", {"start": v(144.25, 19.07) * mm, "mid": v(145.46, 24.75) * mm, "end": v(144.25, 30.44) * mm});
            skArc(sketch, "E99.trimOffspring", {"start": v(137.17, 37.51) * mm, "mid": v(131.49, 38.72) * mm, "end": v(125.8, 37.51) * mm});
            skArc(sketch, "E100.trimOffspring", {"start": v(118.73, 30.44) * mm, "mid": v(117.52, 24.75) * mm, "end": v(118.73, 19.07) * mm});
            skPoint(sketch, "E101.visualSharp", {"position": v(123.05, 35.89) * mm});
            skArc(sketch, "E101.filletArc", {"start": v(120.43, 38.51) * mm, "mid": v(122.96, 37.18) * mm, "end": v(125.8, 37.51) * mm});
            skPoint(sketch, "E102.visualSharp", {"position": v(139.93, 35.89) * mm});
            skArc(sketch, "E102.filletArc", {"start": v(137.17, 37.51) * mm, "mid": v(140.02, 37.18) * mm, "end": v(142.55, 38.51) * mm});
            skPoint(sketch, "E103.visualSharp", {"position": v(142.62, 33.2) * mm});
            skArc(sketch, "E103.filletArc", {"start": v(145.24, 35.82) * mm, "mid": v(143.91, 33.28) * mm, "end": v(144.25, 30.44) * mm});
            skPoint(sketch, "E104.visualSharp", {"position": v(142.62, 16.31) * mm});
            skArc(sketch, "E104.filletArc", {"start": v(144.25, 19.07) * mm, "mid": v(143.91, 16.23) * mm, "end": v(145.24, 13.7) * mm});
            skPoint(sketch, "E105.visualSharp", {"position": v(139.93, 13.62) * mm});
            skArc(sketch, "E105.filletArc", {"start": v(142.55, 11) * mm, "mid": v(140.02, 12.33) * mm, "end": v(137.17, 12) * mm});
            skPoint(sketch, "E106.visualSharp", {"position": v(123.05, 13.62) * mm});
            skArc(sketch, "E106.filletArc", {"start": v(125.8, 12) * mm, "mid": v(122.96, 12.33) * mm, "end": v(120.43, 11) * mm});
            skPoint(sketch, "E107.visualSharp", {"position": v(120.35, 16.31) * mm});
            skArc(sketch, "E107.filletArc", {"start": v(117.73, 13.7) * mm, "mid": v(119.06, 16.23) * mm, "end": v(118.73, 19.07) * mm});
            skPoint(sketch, "E108.visualSharp", {"position": v(120.35, 33.2) * mm});
            skArc(sketch, "E108.filletArc", {"start": v(118.73, 30.44) * mm, "mid": v(119.06, 33.28) * mm, "end": v(117.73, 35.82) * mm});
            skSolve(sketch);
        }
        {
            var Q0;
            {Q0=qUnion([makeQuery(id+"F51.imprint","IMPRINT",FACE,{"disambiguationData":[TD([[makeQuery(id+"F51.imprint","IMPRINT",EDGE,{"derivedFrom":sQuery(id+"F51.wireOp",EDGE,"E73")}),1.0]])]}),makeQuery(id+"F51.imprint","IMPRINT",FACE,{"disambiguationData":[TD([[makeQuery(id+"F51.imprint","IMPRINT",EDGE,{"derivedFrom":sQuery(id+"F51.wireOp",EDGE,"E79.0")}),-1.0]])]}),makeQuery(id+"F51.imprint","IMPRINT",FACE,{"disambiguationData":[TD([[makeQuery(id+"F51.imprint","IMPRINT",EDGE,{"derivedFrom":sQuery(id+"F51.wireOp",EDGE,"E81.0")}),1.0]])]}),makeQuery(id+"F51.imprint","IMPRINT",FACE,{"disambiguationData":[TD([[makeQuery(id+"F51.imprint","IMPRINT",EDGE,{"derivedFrom":sQuery(id+"F51.wireOp",EDGE,"E83.trimOffspring")}),1.0]])]})]);}
            extrude(context, id + "F52", {"entities" : qUnion([Q0]), "operationType" : NewBodyOperationType.REMOVE, "oppositeDirection" : true, "depth" : 5.08 * mm});
        }
        {
            var Q0;
            Q0=makeQuery(id+"F50.opExtrude","CAP_FACE",FACE,{"disambiguationData":[OSD([sQuery(id+"F49.wireOp",EDGE,"E71"),sQuery(id+"F49.wireOp",EDGE,"E72")])],"isStart":true});
            var sketch = newSketch(context, id + "F53", { "sketchPlane" : qUnion([Q0])});
            skLineSegment(sketch, "E109", {"start": v(131.49, -56.88) * mm, "end": v(131.49, 7.13) * mm, "construction": true});
            skPoint(sketch, "E110", {"position": v(131.49, -24.75) * mm});
            skCircle(sketch, "E111", {"center": v(131.49, -24.75) * mm, "radius": 21.59 * mm, "construction": true});
            skCircle(sketch, "E112", {"center": v(131.49, -46.34) * mm, "radius": 2.54 * mm});
            skCircle(sketch, "E113", {"center": v(131.49, -3.16) * mm, "radius": 2.54 * mm});
            skSolve(sketch);
        }
        {
            var Q0;
            {Q0=qUnion([makeQuery(id+"F53.imprint","IMPRINT",FACE,{"disambiguationData":[TD([[makeQuery(id+"F53.imprint","IMPRINT",EDGE,{"derivedFrom":sQuery(id+"F53.wireOp",EDGE,"E112")}),1.0]])]}),makeQuery(id+"F53.imprint","IMPRINT",FACE,{"disambiguationData":[TD([[makeQuery(id+"F53.imprint","IMPRINT",EDGE,{"derivedFrom":sQuery(id+"F53.wireOp",EDGE,"E113")}),1.0]])]})]);}
            extrude(context, id + "F54", {"entities" : qUnion([Q0]), "operationType" : NewBodyOperationType.REMOVE, "endBound" : BoundingType.THROUGH_ALL, "oppositeDirection" : true, "depth" : 25.4 * mm});
        }
        {
            var Q0;
            Q0=qCreatedBy(makeId("Top.planeOp"),FACE);
            var sketch = newSketch(context, id + "F55", { "sketchPlane" : qUnion([Q0])});
            skCircle(sketch, "E114", {"center": v(93.35, 90.54) * mm, "radius": 6.35 * mm});
            skSolve(sketch);
        }
        {
            var Q0;
            Q0=makeQuery(id+"F55.imprint","IMPRINT",FACE,{"disambiguationData":[TD([[makeQuery(id+"F55.imprint","IMPRINT",EDGE,{"derivedFrom":sQuery(id+"F55.wireOp",EDGE,"E114")}),1.0]])]});
            extrude(context, id + "F56", {"entities" : qUnion([Q0]), "depth" : 3.17 * mm});
        }
        {
            var Q0;
            Q0=makeQuery(id+"F56.opExtrude","CAP_FACE",FACE,{"disambiguationData":[OSD([sQuery(id+"F55.wireOp",EDGE,"E114")])],"isStart":false});
            var sketch = newSketch(context, id + "F57", { "sketchPlane" : qUnion([Q0])});
            skCircle(sketch, "E115", {"center": v(93.35, 90.54) * mm, "radius": 5.33 * mm});
            skSolve(sketch);
        }
        {
            var Q0;
            Q0=makeQuery(id+"F57.imprint","IMPRINT",FACE,{"disambiguationData":[TD([[makeQuery(id+"F57.imprint","IMPRINT",EDGE,{"derivedFrom":sQuery(id+"F57.wireOp",EDGE,"E115")}),1.0]])]});
            extrude(context, id + "F58", {"entities" : qUnion([Q0]), "operationType" : NewBodyOperationType.ADD, "depth" : 6.35 * mm});
        }
        {
            var Q0;
            Q0=makeQuery(id+"F58.opExtrude","CAP_FACE",FACE,{"disambiguationData":[OSD([sQuery(id+"F57.wireOp",EDGE,"E115")])],"isStart":false});
            var sketch = newSketch(context, id + "F59", { "sketchPlane" : qUnion([Q0])});
            skCircle(sketch, "E116", {"center": v(93.35, 90.54) * mm, "radius": 3 * mm});
            skSolve(sketch);
        }
        {
            var Q0;
            Q0=makeQuery(id+"F59.imprint","IMPRINT",FACE,{"disambiguationData":[TD([[makeQuery(id+"F59.imprint","IMPRINT",EDGE,{"derivedFrom":sQuery(id+"F59.wireOp",EDGE,"E116")}),1.0]])]});
            extrude(context, id + "F60", {"entities" : qUnion([Q0]), "operationType" : NewBodyOperationType.REMOVE, "endBound" : BoundingType.THROUGH_ALL, "oppositeDirection" : true, "depth" : 25.4 * mm});
        }
        {
            var Q0;
            Q0=qCreatedBy(makeId("Top.planeOp"),FACE);
            var sketch = newSketch(context, id + "F61", { "sketchPlane" : qUnion([Q0])});
            skCircle(sketch, "E117", {"center": v(134.51, 129.38) * mm, "radius": 38.1 * mm});
            skCircle(sketch, "E118", {"center": v(134.51, 129.38) * mm, "radius": 12.5 * mm});
            skCircle(sketch, "E119", {"center": v(134.51, 129.38) * mm, "radius": 21.59 * mm, "construction": true});
            skCircle(sketch, "E120", {"center": v(134.51, 150.97) * mm, "radius": 2.54 * mm});
            skCircle(sketch, "E121", {"center": v(134.51, 107.8) * mm, "radius": 2.54 * mm});
            skSolve(sketch);
        }
        {
            var Q0;
            Q0=makeQuery(id+"F61.imprint","IMPRINT",FACE,{"disambiguationData":[TD([[makeQuery(id+"F61.imprint","IMPRINT",EDGE,{"derivedFrom":sQuery(id+"F61.wireOp",EDGE,"E117")}),1.0]])]});
            extrude(context, id + "F62", {"entities" : qUnion([Q0]), "depth" : 3.17 * mm});
        }
        {
            var Q0;
            Q0=qCreatedBy(makeId("Top.planeOp"),FACE);
            var sketch = newSketch(context, id + "F63", { "sketchPlane" : qUnion([Q0])});
            skCircle(sketch, "E122.cCircle", {"center": v(-79.71, 87.15) * mm, "radius": 3.18 * mm, "construction": true});
            skLineSegment(sketch, "E122.0", {"start": v(-76.05, 87) * mm, "end": v(-78.01, 83.9) * mm});
            skLineSegment(sketch, "E122.1", {"start": v(-78.01, 83.9) * mm, "end": v(-81.67, 84.05) * mm});
            skLineSegment(sketch, "E122.2", {"start": v(-81.67, 84.05) * mm, "end": v(-83.38, 87.3) * mm});
            skLineSegment(sketch, "E122.3", {"start": v(-83.38, 87.3) * mm, "end": v(-81.41, 90.4) * mm});
            skLineSegment(sketch, "E122.4", {"start": v(-81.41, 90.4) * mm, "end": v(-77.75, 90.25) * mm});
            skLineSegment(sketch, "E122.5", {"start": v(-77.75, 90.25) * mm, "end": v(-76.05, 87) * mm});
            skPoint(sketch, "E122.0.midPoint", {"position": v(-77.03, 85.45) * mm});
            skSolve(sketch);
        }
        {
            var Q0;
            Q0=qSketchRegion(id+"F63",true);
            extrude(context, id + "F64", {"entities" : qUnion([Q0]), "depth" : 6.35 * mm});
        }
        {
            var Q0;
            Q0=makeQuery(id+"F64.opExtrude","CAP_FACE",FACE,{"disambiguationData":[OSD([sQuery(id+"F63.wireOp",EDGE,"E122.0"),sQuery(id+"F63.wireOp",EDGE,"E122.1"),sQuery(id+"F63.wireOp",EDGE,"E122.2"),sQuery(id+"F63.wireOp",EDGE,"E122.3"),sQuery(id+"F63.wireOp",EDGE,"E122.4"),sQuery(id+"F63.wireOp",EDGE,"E122.5")])],"isStart":false});
            var sketch = newSketch(context, id + "F65", { "sketchPlane" : qUnion([Q0])});
            skCircle(sketch, "E123", {"center": v(-79.71, 87.15) * mm, "radius": 1.13 * mm});
            skLineSegment(sketch, "E124", {"start": v(-77.75, 90.25) * mm, "end": v(-81.67, 84.05) * mm, "construction": true});
            skLineSegment(sketch, "E125", {"start": v(-82.4, 88.85) * mm, "end": v(-77.03, 85.45) * mm, "construction": true});
            skSolve(sketch);
        }
        {
            var Q0;
            Q0=qSketchRegion(id+"F65",true);
            extrude(context, id + "F66", {"entities" : qUnion([Q0]), "operationType" : NewBodyOperationType.REMOVE, "oppositeDirection" : true, "depth" : 4.76 * mm});
        }
        {
            var Q0;
            Q0=makeQuery(id+"F64.opExtrude","CAP_FACE",FACE,{"disambiguationData":[OSD([sQuery(id+"F63.wireOp",EDGE,"E122.0"),sQuery(id+"F63.wireOp",EDGE,"E122.1"),sQuery(id+"F63.wireOp",EDGE,"E122.2"),sQuery(id+"F63.wireOp",EDGE,"E122.3"),sQuery(id+"F63.wireOp",EDGE,"E122.4"),sQuery(id+"F63.wireOp",EDGE,"E122.5")])],"isStart":true});
            var sketch = newSketch(context, id + "F67", { "sketchPlane" : qUnion([Q0])});
            skCircle(sketch, "E126", {"center": v(-79.71, -87.15) * mm, "radius": 1.13 * mm});
            skLineSegment(sketch, "E127", {"start": v(-82.4, -88.85) * mm, "end": v(-77.03, -85.45) * mm, "construction": true});
            skLineSegment(sketch, "E128", {"start": v(-77.03, -85.45) * mm, "end": v(-77.75, -90.25) * mm, "construction": true});
            skLineSegment(sketch, "E129", {"start": v(-77.75, -90.25) * mm, "end": v(-81.67, -84.05) * mm, "construction": true});
            skSolve(sketch);
        }
        {
            var Q0;
            Q0=qSketchRegion(id+"F67",true);
            extrude(context, id + "F68", {"entities" : qUnion([Q0]), "operationType" : NewBodyOperationType.ADD, "depth" : 4.76 * mm});
        }
        {
            var Q0;
            Q0=makeQuery(id+"F56.opExtrude","CAP_FACE",FACE,{"disambiguationData":[OSD([sQuery(id+"F55.wireOp",EDGE,"E114")])],"isStart":false});
            var sketch = newSketch(context, id + "F69", { "sketchPlane" : qUnion([Q0])});
            skCircle(sketch, "E130", {"center": v(93.35, 90.54) * mm, "radius": 3.81 * mm});
            skCircle(sketch, "E131", {"center": v(93.35, 90.54) * mm, "radius": 7.43 * mm});
            skSolve(sketch);
        }
        {
            var Q0;
            Q0=qSketchRegion(id+"F69",true);
            extrude(context, id + "F70", {"entities" : qUnion([Q0]), "operationType" : NewBodyOperationType.ADD, "depth" : 0.25 * mm});
        }
        {
            var Q0;
            Q0=makeQuery(id+"F46.boolean.opBoolean","COPY",FACE,{"derivedFrom":makeQuery(id+"F46.opExtrude","CAP_FACE",FACE,{"disambiguationData":[OSD([sQuery(id+"F21.wireOp",EDGE,"E21"),sQuery(id+"F21.wireOp",EDGE,"E22"),sQuery(id+"F43.wireOp",EDGE,"E45"),sQuery(id+"F45.wireOp",EDGE,"E53.0"),sQuery(id+"F45.wireOp",EDGE,"E57.trimOffspring"),sQuery(id+"F45.wireOp",EDGE,"E63.trimOffspring"),sQuery(id+"F45.wireOp",EDGE,"E66.trimOffspring")])],"isStart":false})});
            var sketch = newSketch(context, id + "F71", { "sketchPlane" : qUnion([Q0])});
            skLineSegment(sketch, "E132.bottom", {"start": v(58.6, 77.73) * mm, "end": v(50.98, 77.73) * mm});
            skLineSegment(sketch, "E132.top", {"start": v(58.6, 91.7) * mm, "end": v(50.98, 91.7) * mm});
            skLineSegment(sketch, "E132.left", {"start": v(58.6, 77.73) * mm, "end": v(58.6, 91.7) * mm});
            skLineSegment(sketch, "E132.right", {"start": v(50.98, 77.73) * mm, "end": v(50.98, 91.7) * mm});
            skCircle(sketch, "E133.0", {"center": v(54.8, 81.54) * mm, "radius": 2.54 * mm});
            skLineSegment(sketch, "E134", {"start": v(58.6, 81.54) * mm, "end": v(54.8, 81.54) * mm, "construction": true});
            skLineSegment(sketch, "E135", {"start": v(54.8, 81.54) * mm, "end": v(50.98, 81.54) * mm, "construction": true});
            skLineSegment(sketch, "E136", {"start": v(54.8, 81.54) * mm, "end": v(54.8, 77.73) * mm, "construction": true});
            skSolve(sketch);
        }
        {
            var Q0;
            Q0=qSketchRegion(id+"F71",true);
            extrude(context, id + "F72", {"entities" : qUnion([Q0]), "depth" : 0.89 * mm});
        }
        {
            var Q0;
            Q0=makeQuery(id+"F72.opExtrude","CAP_FACE",FACE,{"disambiguationData":[OSD([sQuery(id+"F71.wireOp",EDGE,"E132.bottom"),sQuery(id+"F71.wireOp",EDGE,"E132.top"),sQuery(id+"F71.wireOp",EDGE,"E132.left"),sQuery(id+"F71.wireOp",EDGE,"E132.right"),sQuery(id+"F71.wireOp",EDGE,"E133.0")])],"isStart":false});
            var sketch = newSketch(context, id + "F73", { "sketchPlane" : qUnion([Q0])});
            skLineSegment(sketch, "E137.bottom", {"start": v(58.6, 91.7) * mm, "end": v(50.98, 91.7) * mm});
            skLineSegment(sketch, "E137.top", {"start": v(58.6, 90.8) * mm, "end": v(50.98, 90.8) * mm});
            skLineSegment(sketch, "E137.left", {"start": v(58.6, 91.7) * mm, "end": v(58.6, 90.8) * mm});
            skLineSegment(sketch, "E137.right", {"start": v(50.98, 91.7) * mm, "end": v(50.98, 90.8) * mm});
            skSolve(sketch);
        }
        {
            var Q0;
            Q0=qSketchRegion(id+"F73",true);
            extrude(context, id + "F74", {"entities" : qUnion([Q0]), "operationType" : NewBodyOperationType.ADD, "depth" : 6.35 * mm});
        }
        {
            var Q0;
            Q0=makeQuery(id+"F74.boolean.opBoolean","MERGE",FACE,{"derivedFrom":[makeQuery(id+"F72.opExtrude","SWEPT_FACE",FACE,{"disambiguationData":[OSD([sQuery(id+"F71.wireOp",EDGE,"E132.top")])]}),makeQuery(id+"F74.opExtrude","SWEPT_FACE",FACE,{"disambiguationData":[OSD([sQuery(id+"F73.wireOp",EDGE,"E137.bottom")])]})]});
            var sketch = newSketch(context, id + "F75", { "sketchPlane" : qUnion([Q0])});
            skLineSegment(sketch, "E138.bottom", {"start": v(58.6, -2.16) * mm, "end": v(50.98, -2.16) * mm});
            skLineSegment(sketch, "E138.top", {"start": v(58.6, -1.27) * mm, "end": v(50.98, -1.27) * mm});
            skLineSegment(sketch, "E138.left", {"start": v(58.6, -2.16) * mm, "end": v(58.6, -1.27) * mm});
            skLineSegment(sketch, "E138.right", {"start": v(50.98, -2.16) * mm, "end": v(50.98, -1.27) * mm});
            skSolve(sketch);
        }
        {
            var Q0;
            Q0=qSketchRegion(id+"F75",true);
            extrude(context, id + "F76", {"entities" : qUnion([Q0]), "operationType" : NewBodyOperationType.ADD, "depth" : 1.9 * mm});
        }
        {
            var Q0;
            Q0=makeQuery(id+"F76.boolean.opBoolean","MERGE",FACE,{"derivedFrom":[makeQuery(id+"F74.opExtrude","CAP_FACE",FACE,{"disambiguationData":[OSD([sQuery(id+"F73.wireOp",EDGE,"E137.bottom"),sQuery(id+"F73.wireOp",EDGE,"E137.top"),sQuery(id+"F73.wireOp",EDGE,"E137.left"),sQuery(id+"F73.wireOp",EDGE,"E137.right")])],"isStart":false}),makeQuery(id+"F76.opExtrude","SWEPT_FACE",FACE,{"disambiguationData":[OSD([sQuery(id+"F75.wireOp",EDGE,"E138.bottom")])]})]});
            var sketch = newSketch(context, id + "F77", { "sketchPlane" : qUnion([Q0])});
            skLineSegment(sketch, "E139.bottom", {"start": v(58.6, 93.6) * mm, "end": v(50.98, 93.6) * mm});
            skLineSegment(sketch, "E139.top", {"start": v(58.6, 92.71) * mm, "end": v(50.98, 92.71) * mm});
            skLineSegment(sketch, "E139.left", {"start": v(58.6, 93.6) * mm, "end": v(58.6, 92.71) * mm});
            skLineSegment(sketch, "E139.right", {"start": v(50.98, 93.6) * mm, "end": v(50.98, 92.71) * mm});
            skSolve(sketch);
        }
        {
            var Q0;
            Q0=qSketchRegion(id+"F77",true);
            extrude(context, id + "F78", {"entities" : qUnion([Q0]), "operationType" : NewBodyOperationType.ADD, "depth" : 3.17 * mm});
        }
    });
